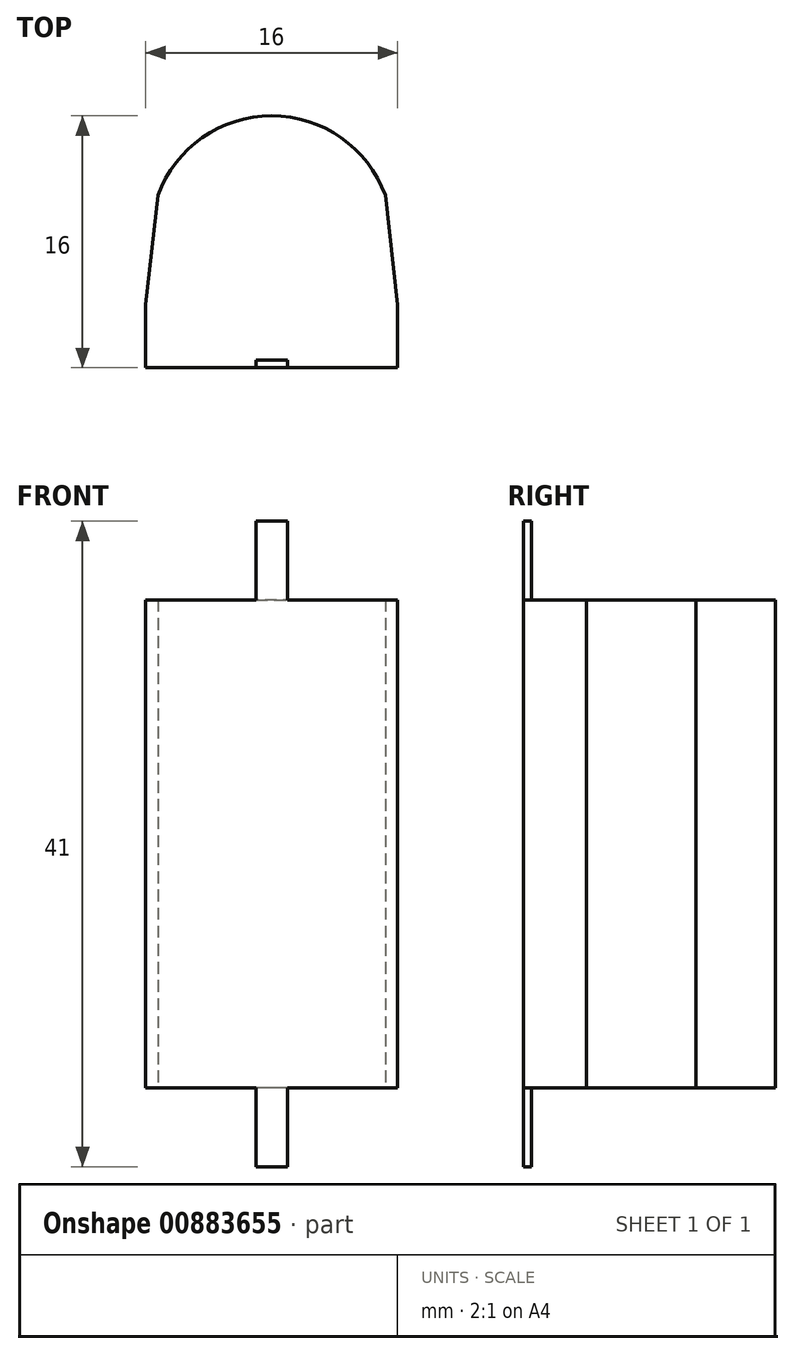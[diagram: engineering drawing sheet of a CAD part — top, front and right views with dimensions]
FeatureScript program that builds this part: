
annotation { "Feature Type Name" : "Feature", "Feature Type Description" : "" }
export const myFeature = defineFeature(function(context is Context, id is Id, definition is map)
    precondition{}
    {
        {
            var Q0;
            Q0=qCreatedBy(makeId("Top.planeOp"),FACE);
            var sketch = newSketch(context, id + "F0", { "sketchPlane" : qUnion([Q0])});
            skLineSegment(sketch, "E0", {"start": v(8, 3.14) * mm, "end": v(-8, 3.14) * mm});
            skLineSegment(sketch, "E1", {"start": v(-8, 3.14) * mm, "end": v(-8, 7.14) * mm});
            skLineSegment(sketch, "E2", {"start": v(-8, 7.14) * mm, "end": v(-7.22, 14.1) * mm});
            skLineSegment(sketch, "E3", {"start": v(8, 3.14) * mm, "end": v(8, 7.14) * mm});
            skLineSegment(sketch, "E4", {"start": v(8, 7.14) * mm, "end": v(7.22, 14.1) * mm});
            skArc(sketch, "E5", {"start": v(7.22, 14.1) * mm, "mid": v(0, 19.14) * mm, "end": v(-7.22, 14.1) * mm});
            skSolve(sketch);
        }
        {
            var Q0;
            Q0=makeQuery(id+"F0.imprint","IMPRINT",FACE,{"disambiguationData":[TD([[makeQuery(id+"F0.imprint","IMPRINT",EDGE,{"derivedFrom":sQuery(id+"F0.wireOp",EDGE,"E0")}),-1.0]])]});
            extrude(context, id + "F1", {"entities" : qUnion([Q0]), "depth" : 31 * mm, "offsetDistance" : 25 * mm});
        }
        {
            var Q0;
            Q0=makeQuery(id+"F1.opExtrude","CAP_FACE",FACE,{"disambiguationData":[OSD([sQuery(id+"F0.wireOp",EDGE,"E0"),sQuery(id+"F0.wireOp",EDGE,"E1"),sQuery(id+"F0.wireOp",EDGE,"E2"),sQuery(id+"F0.wireOp",EDGE,"E3"),sQuery(id+"F0.wireOp",EDGE,"E4"),sQuery(id+"F0.wireOp",EDGE,"E5")])],"isStart":false});
            var sketch = newSketch(context, id + "F2", { "sketchPlane" : qUnion([Q0])});
            skLineSegment(sketch, "E6.bottom", {"start": v(-1, 3.64) * mm, "end": v(1, 3.64) * mm});
            skLineSegment(sketch, "E6.top", {"start": v(-1, 3.14) * mm, "end": v(1, 3.14) * mm});
            skLineSegment(sketch, "E6.left", {"start": v(-1, 3.64) * mm, "end": v(-1, 3.14) * mm});
            skLineSegment(sketch, "E6.right", {"start": v(1, 3.64) * mm, "end": v(1, 3.14) * mm});
            skSolve(sketch);
        }
        {
            var Q0;
            Q0=makeQuery(id+"F2.imprint","IMPRINT",FACE,{"disambiguationData":[TD([[makeQuery(id+"F2.imprint","IMPRINT",EDGE,{"derivedFrom":sQuery(id+"F2.wireOp",EDGE,"E6.bottom")}),-1.0]])]});
            extrude(context, id + "F3", {"entities" : qUnion([Q0]), "operationType" : NewBodyOperationType.ADD, "depth" : 5 * mm, "offsetDistance" : 25 * mm});
        }
        {
            var Q0;
            Q0=makeQuery(id+"F1.opExtrude","CAP_FACE",FACE,{"disambiguationData":[OSD([sQuery(id+"F0.wireOp",EDGE,"E0"),sQuery(id+"F0.wireOp",EDGE,"E1"),sQuery(id+"F0.wireOp",EDGE,"E2"),sQuery(id+"F0.wireOp",EDGE,"E3"),sQuery(id+"F0.wireOp",EDGE,"E4"),sQuery(id+"F0.wireOp",EDGE,"E5")])],"isStart":true});
            var sketch = newSketch(context, id + "F4", { "sketchPlane" : qUnion([Q0])});
            skLineSegment(sketch, "E7.bottom", {"start": v(1, -3.14) * mm, "end": v(-1, -3.14) * mm});
            skLineSegment(sketch, "E7.top", {"start": v(1, -3.64) * mm, "end": v(-1, -3.64) * mm});
            skLineSegment(sketch, "E7.left", {"start": v(1, -3.14) * mm, "end": v(1, -3.64) * mm});
            skLineSegment(sketch, "E7.right", {"start": v(-1, -3.14) * mm, "end": v(-1, -3.64) * mm});
            skSolve(sketch);
        }
        {
            var Q0;
            Q0 = qSketchRegion(id + "F4", true);
            extrude(context, id + "F5", {"entities" : qUnion([Q0]), "operationType" : NewBodyOperationType.ADD, "depth" : 5 * mm, "offsetDistance" : 25 * mm});
        }
    });
